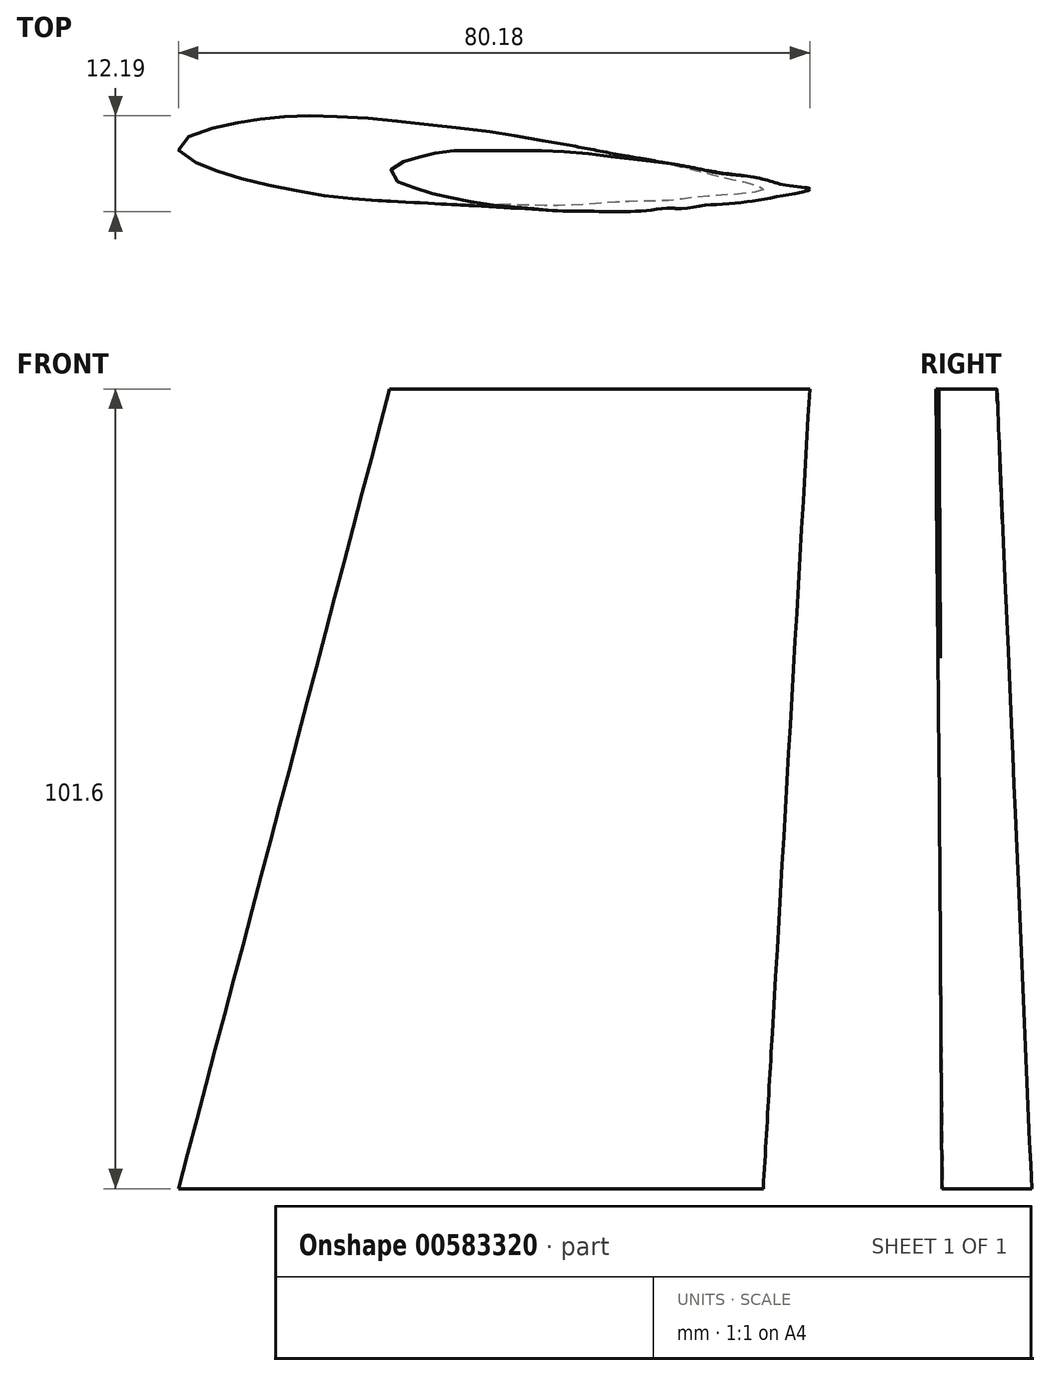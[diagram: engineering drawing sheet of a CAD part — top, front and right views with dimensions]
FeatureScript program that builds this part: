
annotation { "Feature Type Name" : "Feature", "Feature Type Description" : "" }
export const myFeature = defineFeature(function(context is Context, id is Id, definition is map)
    precondition{}
    {
        {
            var Q0;
            Q0=qCreatedBy(makeId("Top.planeOp"),FACE);
            var sketch = newSketch(context, id + "F0", { "sketchPlane" : qUnion([Q0])});
            skFitSpline(sketch, "E0", {"points": [v(0.6, 1.37) * mm, v(3.64, 2.7) * mm, v(7.74, 3.65) * mm, v(10.65, 4.08) * mm, v(14.25, 4.41) * mm, v(18.18, 4.41) * mm, v(23.6, 4.17) * mm, v(28.9, 3.66) * mm, v(35, 2.95) * mm, v(40.17, 2.37) * mm, v(43.85, 1.68) * mm, v(49.93, 0.65) * mm, v(55.4, -0.46) * mm, v(59.25, -1.06) * mm, v(63.5, -1.95) * mm, v(68.15, -3.11) * mm, v(71.23, -3.83) * mm, v(74.23, -4.9) * mm, v(70.22, -5.56) * mm, v(66.04, -5.86) * mm, v(62.03, -6.32) * mm, v(58.1, -6.41) * mm, v(54.13, -6.61) * mm, v(49.35, -6.92) * mm, v(45.18, -6.92) * mm, v(39.79, -6.82) * mm, v(35.2, -6.82) * mm, v(31.24, -6.61) * mm, v(27.07, -6.41) * mm, v(23.3, -6.2) * mm, v(18.62, -5.7) * mm, v(13.94, -4.88) * mm, v(9.27, -3.88) * mm, v(5.35, -2.7) * mm, v(2.35, -1.59) * mm, v(0, 0) * mm, v(0.6, 1.37) * mm]});
            skSolve(sketch);
        }
        {
            var Q0;
            Q0=qCreatedBy(makeId("Top.planeOp"),FACE);
            cPlane(context, id + "F1", {"entities" : qUnion([Q0]), "cplaneType" : CPlaneType.OFFSET, "offset" : 101.6 * mm, "width" : 152.4 * mm, "height" : 152.4 * mm});
        }
        {
            var Q0;
            Q0=qCreatedBy(id+"F1.planeOp",FACE);
            var sketch = newSketch(context, id + "F2", { "sketchPlane" : qUnion([Q0])});
            skFitSpline(sketch, "E1", {"points": [v(27.2, -2.1) * mm, v(28.01, -1.58) * mm, v(29.3, -1.15) * mm, v(30.37, -0.8) * mm, v(31.65, -0.47) * mm, v(32.92, -0.22) * mm, v(34.56, 0) * mm, v(36.74, 0) * mm, v(38.41, 0) * mm, v(40.9, 0) * mm, v(43.59, 0.05) * mm, v(45.68, 0.05) * mm, v(47.78, -0.04) * mm, v(50.73, -0.25) * mm, v(53.21, -0.5) * mm, v(55.57, -0.8) * mm, v(57.96, -1.07) * mm, v(60.06, -1.36) * mm, v(61.81, -1.53) * mm, v(64, -1.89) * mm, v(66.55, -2.4) * mm, v(68.89, -2.86) * mm, v(72.14, -3.21) * mm, v(74.84, -3.77) * mm, v(77.28, -4.38) * mm, v(80.13, -4.84) * mm, v(78.66, -5.35) * mm, v(76.04, -5.8) * mm, v(73.5, -6.3) * mm, v(71.27, -6.57) * mm, v(68.73, -6.8) * mm, v(66.52, -6.94) * mm, v(64.2, -7.32) * mm, v(62.02, -7.28) * mm, v(59.88, -7.54) * mm, v(57.64, -7.69) * mm, v(55.25, -7.74) * mm, v(53.22, -7.69) * mm, v(51.54, -7.69) * mm, v(49.1, -7.64) * mm, v(46.96, -7.54) * mm, v(45.43, -7.38) * mm, v(43.8, -7.23) * mm, v(41.97, -7.08) * mm, v(39.68, -6.9) * mm, v(37.2, -6.47) * mm, v(35.26, -6.05) * mm, v(33.5, -5.75) * mm, v(31.91, -5.32) * mm, v(30.3, -4.78) * mm, v(28.85, -4.35) * mm, v(27.57, -3.8) * mm, v(26.77, -2.86) * mm, v(27.2, -2.1) * mm]});
            skSolve(sketch);
        }
        {
            var Q0;
            Q0=makeQuery(id+"F0.imprint","IMPRINT",FACE,{"disambiguationData":[TD([[makeQuery(id+"F0.imprint","IMPRINT",EDGE,{"derivedFrom":sQuery(id+"F0.wireOp",EDGE,"E0")}),-1.0]])]});
            var Q1;
            Q1=makeQuery(id+"F2.imprint","IMPRINT",FACE,{"disambiguationData":[TD([[makeQuery(id+"F2.imprint","IMPRINT",EDGE,{"derivedFrom":sQuery(id+"F2.wireOp",EDGE,"E1")}),-1.0]])]});
            var Q2;
            Q2=sQuery(id+"F0.wireOp",VERTEX,"E0.17.internal");
            var Q3;
            Q3=sQuery(id+"F2.wireOp",VERTEX,"E1.25.internal");
            loft(context, id + "F3", {"sheetProfilesArray" : [{ "sheetProfileEntities" : qUnion([Q0]) }, { "sheetProfileEntities" : qUnion([Q1]) }], "matchConnections" : true, "connections" : [{ "connectionEntities" : qUnion([Q2, Q3]), "connectionEdgeQueries" : qUnion([]), "connectionEdgeParameters" : [] }]});
        }
    });
